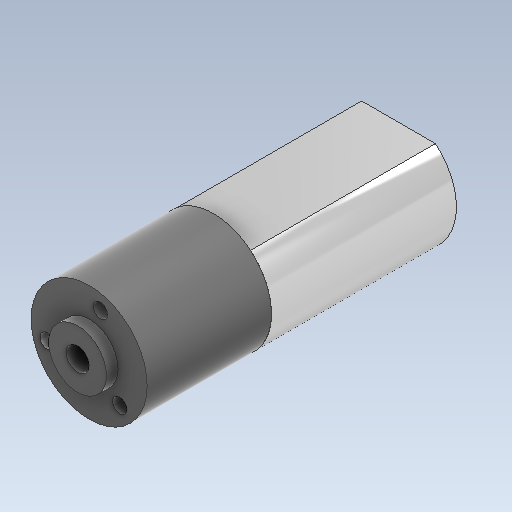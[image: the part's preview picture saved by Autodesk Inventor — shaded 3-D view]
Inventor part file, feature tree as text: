
AUTODESK INVENTOR PART (.ipt)
format: ipt  version: 2020 (Build 240168000, 168)  size: 188,928 bytes
history: native  units: mm
features: extrude x7, sketch x7, other x1, fillet x1
ambient origin geometry x8: Origin, YZ Plane, XZ Plane, XY Plane, X Axis, Y Axis, Z Axis, Center Point
bodies: Body1 (feature_tree)
feature tree (16):
  other  "Твердое тело1"
  extrude  "Выдавливание1"  Depth=20.05mm
  extrude  "Выдавливание2"  Depth=21.5mm TaperAngle=0.0deg
  extrude  "Выдавливание3"  Depth=10.0mm
  extrude  "Выдавливание4"  Depth=2.0mm TaperAngle=0.0deg
  extrude  "Выдавливание5"  Depth=20.0mm
  fillet  "Сопряжение1"  Radius=32.0mm
  extrude  "Выдавливание6"  Depth=15.4mm
  extrude  "Выдавливание7"  Depth=15.0mm
  sketch  "Эскиз1"
  sketch  "Эскиз2"
  sketch  "Эскиз3"
  sketch  "Эскиз4"
  sketch  "Эскиз5"
  sketch  "Эскиз6"
  sketch  "Эскиз7"
